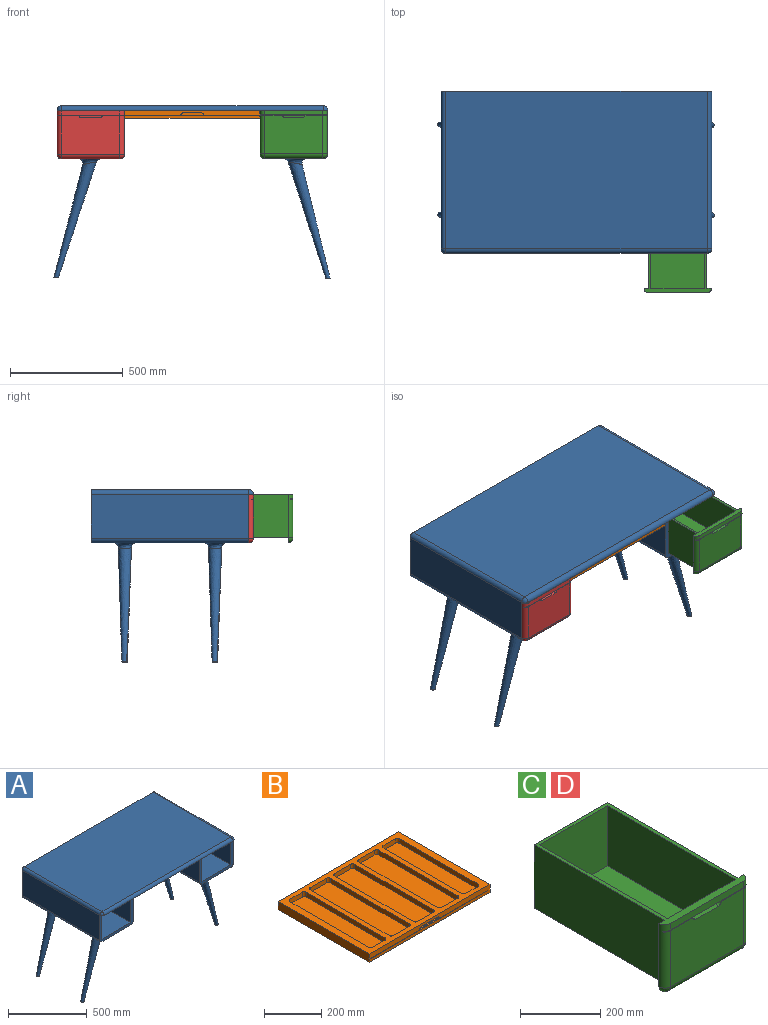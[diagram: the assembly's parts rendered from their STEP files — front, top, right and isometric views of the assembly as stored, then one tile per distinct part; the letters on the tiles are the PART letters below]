
ASSEMBLY  parts=4 mates=3
PART A: 42 faces, bbox 1230x720x774.7 mm
  f0: plane 1200x235mm, normal (0,1,0), area 152485mm2, adj f4,f5,f6,f7,f8,f9,f10,f14
  f1: plane 300x215mm, normal (0,-1,0), area 13628.3mm2, adj f4,f10,f11,f12,f13,f14,f15,f16
  f2: plane 300x215mm, normal (0,-1,0), area 13629.8mm2, adj f3,f5,f9,f17,f18,f19,f20,f21
  f3: plane 695x0.2mm, normal (0,0,-1), area 140.7mm2, adj f2,f22,f24,f38
  f4: plane 700x260mm, normal (0,0,-1), area 166497.4mm2, adj f0,f1,f15,f16,f35,f36
  f5: plane 700x260mm, normal (0,0,-1), area 166517.7mm2, adj f0,f2,f17,f18,f29,f30
  f6: cylinder r=20mm len=700mm, axis (0,1,0), area 21991.1mm2, adj f0,f7,f10,f39
  f7: plane 1160x700mm, normal (0,0,1), area 812000mm2, adj f0,f6,f8,f40
  f8: cylinder r=20mm len=700mm, axis (0,1,0), area 21991.1mm2, adj f0,f7,f9,f41
  f9: plane 700x195mm, normal (-1,0,0), area 136500mm2, adj f0,f2,f8,f17
  f10: plane 700x195mm, normal (1,0,0), area 136500mm2, adj f0,f1,f6,f16
  f11: plane 695x195mm, normal (-1,0,0), area 135525mm2, adj f1,f12,f23,f37
  f12: plane 695x260mm, normal (0,0,1), area 180700mm2, adj f1,f11,f13,f23
  f13: plane 695x195mm, normal (1,0,0), area 135525mm2, adj f1,f12,f23,f37
  f14: plane 700x195mm, normal (-1,0,0), area 136500mm2, adj f0,f1,f15,f37
  f15: cylinder r=20mm len=700mm, axis (0,1,0), area 21991.1mm2, adj f0,f1,f4,f14
  f16: cylinder r=20mm len=700mm, axis (0,1,0), area 21991.1mm2, adj f0,f1,f4,f10
  f17: cylinder r=20mm len=700mm, axis (0,1,0), area 21991.1mm2, adj f0,f2,f5,f9
  f18: cylinder r=20mm len=700mm, axis (0,1,0), area 21991.1mm2, adj f0,f2,f5,f19
  f19: plane 700x195mm, normal (1,0,0), area 136500mm2, adj f0,f2,f18,f37
  f20: plane 695x195mm, normal (-1,0,0), area 135525mm2, adj f2,f21,f24,f37
  f21: plane 695x260mm, normal (0,0,1), area 180700mm2, adj f2,f20,f22,f24
  f22: plane 695x180mm, normal (1,0,0), area 125100mm2, adj f2,f3,f21,f24
  f23: plane 260x195mm, normal (0,-1,0), area 50700mm2, adj f11,f12,f13,f37
  f24: plane 260x195mm, normal (0,-1,0), area 50698.5mm2, adj f3,f20,f21,f22,f37,f38
  f25: plane 21.6x20mm, normal (0,0,-1), area 338.3mm2, adj f26
  f26: bspline ~525.16x192.21mm, area 64810.1mm2, adj f25,f30
  f27: plane 21.6x20mm, normal (0,0,-1), area 338.3mm2, adj f28
  f28: bspline ~525.16x192.21mm, area 64810.1mm2, adj f27,f29
  f29: bspline ~100.07x98.52mm, area 7160.3mm2, adj f5,f28
  f30: bspline ~100.07x98.52mm, area 7160.3mm2, adj f5,f26
  f31: plane 21.63x20.1mm, normal (0,0,-1), area 339.8mm2, adj f32
  f32: bspline ~525.78x188.77mm, area 64891.2mm2, adj f31,f35
  f33: plane 21.63x20.1mm, normal (0,0,-1), area 339.5mm2, adj f34
  f34: bspline ~525.78x188.77mm, area 64891.2mm2, adj f33,f36
  f35: bspline ~100.13x98.61mm, area 7157.1mm2, adj f4,f32
  f36: bspline ~100.13x98.61mm, area 7157.1mm2, adj f4,f34
  f37: plane 1200x720mm, normal (0,0,-1), area 805228.3mm2, adj f0,f1,f2,f11,f13,f14,f19,f20
  f38: plane 695x15mm, normal (1,0,0.01), area 10425.9mm2, adj f2,f3,f24,f37
  f39: sphere r=20mm, area 628.3mm2, adj f6,f37,f40
  f40: cylinder r=20mm len=1160mm, axis (-1,0,0), area 36442.5mm2, adj f7,f37,f39,f41
  f41: sphere r=20mm, area 628.3mm2, adj f8,f37,f40
PART B: 61 faces, bbox 598x450x35 mm
  f0: plane 249x5mm, normal (0,0,-1), area 1245mm2, adj f1,f2,f55,f59
  f1: plane 598x21.11mm, normal (0,-1,0), area 11666.7mm2, adj f0,f2,f3,f4,f53,f56,f59,f60
  f2: plane 450x35mm, normal (1,0,0), area 15745.6mm2, adj f0,f1,f3,f5,f6,f7,f54,f55
  f3: plane 598x450mm, normal (0,0,1), area 80929.2mm2, adj f1,f2,f4,f6,f8,f9,f10,f11
  f4: plane 450x35mm, normal (-1,0,0), area 15740mm2, adj f1,f3,f5,f6,f7,f53,f54,f55
  f5: plane 598x450mm, normal (0,0,-1), area 269100mm2, adj f2,f4,f6,f7
  f6: plane 598x35mm, normal (0,1,0), area 20930mm2, adj f2,f3,f4,f5
  f7: plane 598x13mm, normal (0,-1,0), area 7442.1mm2, adj f2,f4,f5,f54
  f8: plane 390x20mm, normal (1,0,0), area 7800mm2, adj f3,f12,f35,f50
  f9: plane 80x20mm, normal (0,-1,0), area 1600mm2, adj f3,f12,f45,f50
  f10: plane 390x20mm, normal (-1,0,0), area 7800mm2, adj f3,f12,f40,f45
  f11: plane 80x20mm, normal (0,1,0), area 1600mm2, adj f3,f12,f35,f40
  f12: plane 410x100mm, normal (0,0,1), area 40914.2mm2, adj f8,f9,f10,f11,f35,f40,f45,f50
  f13: plane 80x20mm, normal (0,1,0), area 1600mm2, adj f3,f17,f36,f41
  f14: plane 390x20mm, normal (1,0,0), area 7800mm2, adj f3,f17,f36,f49
  f15: plane 80x20mm, normal (0,-1,0), area 1600mm2, adj f3,f17,f44,f49
  f16: plane 390x20mm, normal (-1,0,0), area 7800mm2, adj f3,f17,f41,f44
  f17: plane 410x100mm, normal (0,0,1), area 40914.2mm2, adj f13,f14,f15,f16,f36,f41,f44,f49
  f18: plane 390x20mm, normal (-1,0,0), area 7800mm2, adj f3,f22,f39,f46
  f19: plane 80x20mm, normal (0,1,0), area 1600mm2, adj f3,f22,f34,f39
  f20: plane 390x20mm, normal (1,0,0), area 7800mm2, adj f3,f22,f34,f51
  f21: plane 80x20mm, normal (0,-1,0), area 1600mm2, adj f3,f22,f46,f51
  f22: plane 410x100mm, normal (0,0,1), area 40914.2mm2, adj f18,f19,f20,f21,f34,f39,f46,f51
  f23: plane 390x20mm, normal (-1,0,0), area 7800mm2, adj f3,f27,f42,f43
  f24: plane 60x20mm, normal (0,1,0), area 1200mm2, adj f3,f27,f37,f42
  f25: plane 390x20mm, normal (1,0,0), area 7800mm2, adj f3,f27,f37,f48
  f26: plane 60x20mm, normal (0,-1,0), area 1200mm2, adj f3,f27,f43,f48
  f27: plane 410x80mm, normal (0,0,1), area 32714.2mm2, adj f23,f24,f25,f26,f37,f42,f43,f48
  f28: plane 60x20mm, normal (0,1,0), area 1200mm2, adj f3,f32,f33,f38
  f29: plane 390x20mm, normal (1,0,0), area 7800mm2, adj f3,f32,f33,f52
  f30: plane 60x20mm, normal (0,-1,0), area 1200mm2, adj f3,f32,f47,f52
  f31: plane 390x20mm, normal (-1,0,0), area 7800mm2, adj f3,f32,f38,f47
  f32: plane 410x80mm, normal (0,0,1), area 32714.2mm2, adj f28,f29,f30,f31,f33,f38,f47,f52
  f33: cylinder r=10mm len=20mm, axis (0,0,-1), area 314.2mm2, adj f3,f28,f29,f32
  f34: cylinder r=10mm len=20mm, axis (0,0,-1), area 314.2mm2, adj f3,f19,f20,f22
  f35: cylinder r=10mm len=20mm, axis (0,0,-1), area 314.2mm2, adj f3,f8,f11,f12
  f36: cylinder r=10mm len=20mm, axis (0,0,-1), area 314.2mm2, adj f3,f13,f14,f17
  f37: cylinder r=10mm len=20mm, axis (0,0,-1), area 314.2mm2, adj f3,f24,f25,f27
  f38: cylinder r=10mm len=20mm, axis (0,0,-1), area 314.2mm2, adj f3,f28,f31,f32
  f39: cylinder r=10mm len=20mm, axis (0,0,-1), area 314.2mm2, adj f3,f18,f19,f22
  f40: cylinder r=10mm len=20mm, axis (0,0,-1), area 314.2mm2, adj f3,f10,f11,f12
  f41: cylinder r=10mm len=20mm, axis (0,0,-1), area 314.2mm2, adj f3,f13,f16,f17
  f42: cylinder r=10mm len=20mm, axis (0,0,-1), area 314.2mm2, adj f3,f23,f24,f27
  f43: cylinder r=10mm len=20mm, axis (0,0,-1), area 314.2mm2, adj f3,f23,f26,f27
  f44: cylinder r=10mm len=20mm, axis (0,0,-1), area 314.2mm2, adj f3,f15,f16,f17
  f45: cylinder r=10mm len=20mm, axis (0,0,-1), area 314.2mm2, adj f3,f9,f10,f12
  f46: cylinder r=10mm len=20mm, axis (0,0,-1), area 314.2mm2, adj f3,f18,f21,f22
  f47: cylinder r=10mm len=20mm, axis (0,0,-1), area 314.2mm2, adj f3,f30,f31,f32
  f48: cylinder r=10mm len=20mm, axis (0,0,-1), area 314.2mm2, adj f3,f25,f26,f27
  f49: cylinder r=10mm len=20mm, axis (0,0,-1), area 314.2mm2, adj f3,f14,f15,f17
  f50: cylinder r=10mm len=20mm, axis (0,0,-1), area 314.2mm2, adj f3,f8,f9,f12
  f51: cylinder r=10mm len=20mm, axis (0,0,-1), area 314.2mm2, adj f3,f20,f21,f22
  f52: cylinder r=10mm len=20mm, axis (0,0,-1), area 314.2mm2, adj f3,f29,f30,f32
  f53: plane 249x5mm, normal (0,0,-1), area 1245mm2, adj f1,f4,f55,f60
  f54: plane 598x5mm, normal (0,0,1), area 2990mm2, adj f2,f4,f7,f55
  f55: plane 598x2mm, normal (0,-1,0), area 864.1mm2, adj f0,f2,f4,f53,f54,f57
  f56: plane 80x15mm, normal (0,0,-1), area 1200mm2, adj f1,f58,f59,f60
  f57: plane 100x10mm, normal (0,0,1), area 1000mm2, adj f55,f58,f59,f60
  f58: plane 100x10mm, normal (0,-1,0), area 957.1mm2, adj f56,f57,f59,f60
  f59: cylinder r=10mm len=15mm, axis (0,1,0), area 235.6mm2, adj f0,f1,f56,f57,f58
  f60: cylinder r=10mm len=15mm, axis (0,1,0), area 235.6mm2, adj f1,f53,f56,f57,f58
PART C: 28 faces, bbox 298x480x213 mm
  f0: plane 460x193mm, normal (-1,0,0), area 88780mm2, adj f4,f5,f12,f27
  f1: plane 460x193mm, normal (1,0,0), area 88780mm2, adj f4,f5,f12,f27
  f2: plane 96.32x10mm, normal (0,0,1), area 912.8mm2, adj f11,f15,f18,f21,f22
  f3: plane 258x20mm, normal (0,-1,0), area 5160mm2, adj f13,f22,f23,f27
  f4: plane 460x258mm, normal (0,0,-1), area 118680mm2, adj f0,f1,f5,f12
  f5: plane 258x193mm, normal (0,1,0), area 49794mm2, adj f0,f1,f4,f27
  f6: plane 450x183mm, normal (1,0,0), area 82350mm2, adj f7,f9,f10,f27
  f7: plane 450x238mm, normal (0,0,1), area 107100mm2, adj f6,f8,f9,f10
  f8: plane 450x183mm, normal (-1,0,0), area 82350mm2, adj f7,f9,f10,f27
  f9: plane 238x183mm, normal (0,1,0), area 42596.9mm2, adj f6,f7,f8,f16,f17,f18,f19,f27
  f10: plane 238x183mm, normal (0,-1,0), area 43554mm2, adj f6,f7,f8,f27
  f11: plane 258x171mm, normal (0,-1,0), area 43160.9mm2, adj f2,f14,f16,f18,f19,f22,f23,f24
  f12: plane 298x213mm, normal (0,1,0), area 13508.3mm2, adj f0,f1,f4,f22,f23,f24,f25,f26
  f13: plane 292.64x10mm, normal (0,0,-1), area 2825.7mm2, adj f3,f15,f21,f22,f23
  f14: plane 96.32x10mm, normal (0,0,1), area 912.8mm2, adj f11,f15,f19,f23
  f15: plane 275.32x2mm, normal (0,-1,0), area 550.6mm2, adj f2,f13,f14,f17,f20,f23
  f16: plane 80x20mm, normal (0,0,1), area 1600mm2, adj f9,f11,f18,f19
  f17: plane 100x10mm, normal (0,0,-1), area 1000mm2, adj f9,f15,f18,f19
  f18: cylinder r=10mm len=20mm, axis (0,1,0), area 314.2mm2, adj f2,f9,f11,f16,f17
  f19: cylinder r=10mm len=20mm, axis (0,1,0), area 314.2mm2, adj f9,f11,f14,f16,f17
  f20: plane 2x1mm, normal (-1,0,0), area 1.6mm2, adj f15,f21
  f21: cylinder r=1mm len=17.32mm, axis (-1,0,0), area 53.2mm2, adj f2,f13,f20,f22
  f22: cylinder r=20mm len=193mm, axis (0,0,-1), area 6023.2mm2, adj f2,f3,f11,f12,f13,f21,f26,f27
  f23: cylinder r=20mm len=193mm, axis (0,0,1), area 6021.4mm2, adj f3,f11,f12,f13,f14,f15,f25,f27
  f24: cylinder r=20mm len=258mm, axis (-1,0,0), area 8105.3mm2, adj f11,f12,f25,f26
  f25: sphere r=20mm, area 628.3mm2, adj f12,f23,f24
  f26: sphere r=20mm, area 628.3mm2, adj f12,f22,f24
  f27: plane 480x298mm, normal (0,0,1), area 17368.3mm2, adj f0,f1,f3,f5,f6,f8,f9,f10
PART D: same geometry as C
PLACE A t=(-192.63,-1232.42,-1365.43)mm
PLACE B t=(107.37,-1482.42,-1385.43)mm
PLACE C t=(737.37,-1657.23,-1533.43)mm
PLACE D t=(-161.63,-1482.42,-1535.43)mm
MATE fastened A.f13 <-> C.f0  axis (1,0,0) through (727.37,-1647.23,-1350.43)mm
MATE fastened A.f40 <-> B.f4  axis (1,0,0) through (107.37,-1932.42,-1350.43)mm
MATE fastened A.f2 <-> D.f12  axis (0,-1,0) through (-42.63,-1932.42,-1545.43)mm
